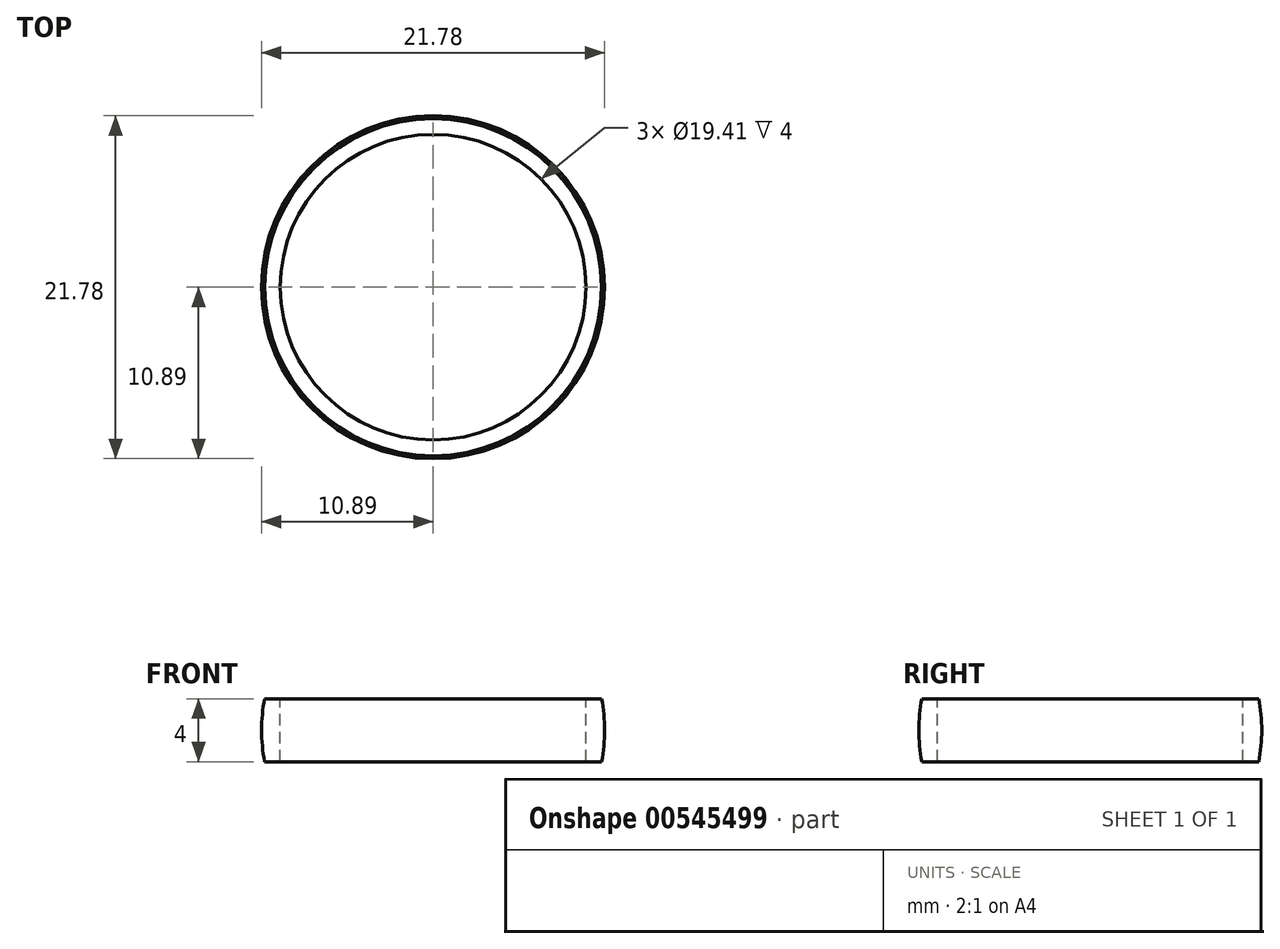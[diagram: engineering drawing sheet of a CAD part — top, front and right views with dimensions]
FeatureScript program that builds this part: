
annotation { "Feature Type Name" : "Feature", "Feature Type Description" : "" }
export const myFeature = defineFeature(function(context is Context, id is Id, definition is map)
    precondition{}
    {
        {
            var Q0;
            Q0=qCreatedBy(makeId("Front.planeOp"),FACE);
            var sketch = newSketch(context, id + "F0", { "sketchPlane" : qUnion([Q0])});
            skArc(sketch, "E0", {"start": v(10.7, -2) * mm, "mid": v(10.9, 0) * mm, "end": v(10.7, 2) * mm});
            skLineSegment(sketch, "E1", {"start": v(10.7, 2) * mm, "end": v(9.7, 2) * mm});
            skLineSegment(sketch, "E2", {"start": v(10.7, -2) * mm, "end": v(9.7, -2) * mm});
            skLineSegment(sketch, "E3", {"start": v(9.7, -2) * mm, "end": v(9.7, 2) * mm});
            skLineSegment(sketch, "E4", {"start": v(0, 7.87) * mm, "end": v(0, -8.1) * mm});
            skSolve(sketch);
        }
        {
            var Q0;
            Q0 = qSketchRegion(id + "F0", true);
            var Q1;
            Q1=sQuery(id+"F0.wireOp",EDGE,"E4");
            revolve(context, id + "F1", {"entities" : qUnion([Q0]), "axis" : qUnion([Q1]), "revolveType" : RevolveType.FULL});
        }
    });
